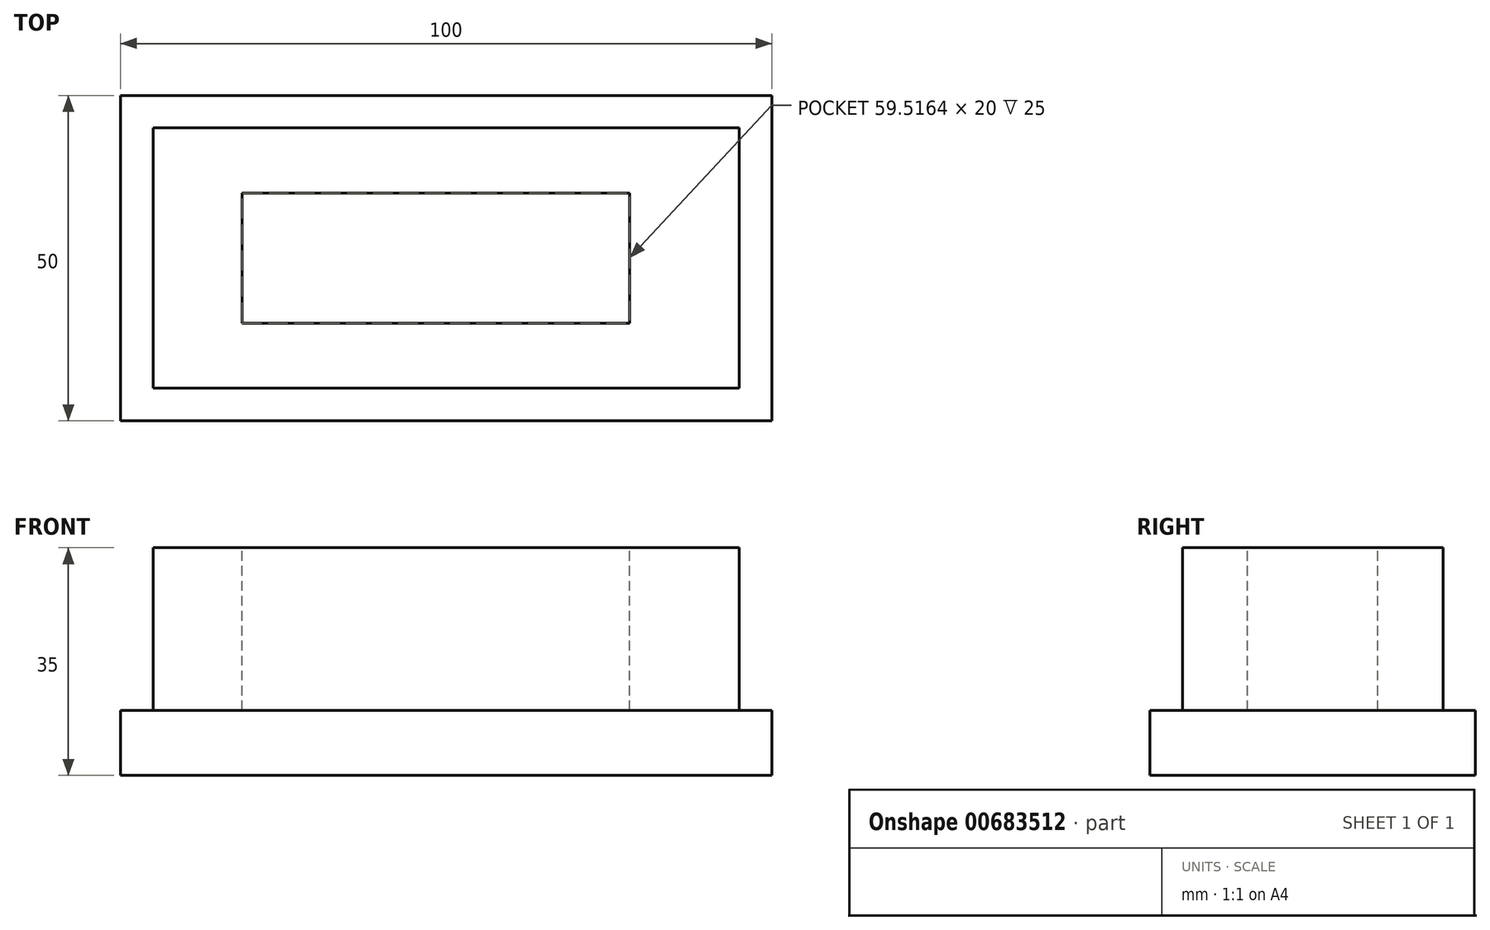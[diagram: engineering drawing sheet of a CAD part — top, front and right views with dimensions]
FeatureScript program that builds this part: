
annotation { "Feature Type Name" : "Feature", "Feature Type Description" : "" }
export const myFeature = defineFeature(function(context is Context, id is Id, definition is map)
    precondition{}
    {
        {
            var Q0;
            Q0=qCreatedBy(makeId("Top.planeOp"),FACE);
            var sketch = newSketch(context, id + "F0", { "sketchPlane" : qUnion([Q0])});
            skLineSegment(sketch, "E0.bottom", {"start": v(-50.38, -7.52) * mm, "end": v(49.62, -7.52) * mm});
            skLineSegment(sketch, "E0.top", {"start": v(-50.38, -57.52) * mm, "end": v(49.62, -57.52) * mm});
            skLineSegment(sketch, "E0.left", {"start": v(-50.38, -7.52) * mm, "end": v(-50.38, -57.52) * mm});
            skLineSegment(sketch, "E0.right", {"start": v(49.62, -7.52) * mm, "end": v(49.62, -57.52) * mm});
            skSolve(sketch);
        }
        {
            var Q0;
            Q0 = qSketchRegion(id + "F0", true);
            extrude(context, id + "F1", {"entities" : qUnion([Q0]), "depth" : 10 * mm, "offsetDistance" : 25 * mm});
        }
        {
            var Q0;
            Q0=makeQuery(id+"F1.opExtrude","CAP_FACE",FACE,{"disambiguationData":[OSD([sQuery(id+"F0.wireOp",EDGE,"E0.bottom"),sQuery(id+"F0.wireOp",EDGE,"E0.top"),sQuery(id+"F0.wireOp",EDGE,"E0.left"),sQuery(id+"F0.wireOp",EDGE,"E0.right")])],"isStart":false});
            var sketch = newSketch(context, id + "F2", { "sketchPlane" : qUnion([Q0])});
            skLineSegment(sketch, "E1.bottom", {"start": v(-45.38, -12.52) * mm, "end": v(44.62, -12.52) * mm});
            skLineSegment(sketch, "E1.top", {"start": v(-45.38, -52.52) * mm, "end": v(44.62, -52.52) * mm});
            skLineSegment(sketch, "E1.left", {"start": v(-45.38, -12.52) * mm, "end": v(-45.38, -52.52) * mm});
            skLineSegment(sketch, "E1.right", {"start": v(44.62, -12.52) * mm, "end": v(44.62, -52.52) * mm});
            skSolve(sketch);
        }
        {
            var Q0;
            Q0=makeQuery(id+"F2.imprint","IMPRINT",FACE,{"disambiguationData":[TD([[makeQuery(id+"F2.imprint","IMPRINT",EDGE,{"derivedFrom":sQuery(id+"F2.wireOp",EDGE,"E1.bottom")}),-1.0]])]});
            extrude(context, id + "F3", {"entities" : qUnion([Q0]), "operationType" : NewBodyOperationType.ADD, "depth" : 5 * mm, "offsetDistance" : 25 * mm});
        }
        {
            var Q0;
            Q0=makeQuery(id+"F2.imprint","IMPRINT",FACE,{"disambiguationData":[TD([[makeQuery(id+"F2.imprint","IMPRINT",EDGE,{"derivedFrom":sQuery(id+"F2.wireOp",EDGE,"E1.bottom")}),-1.0]])]});
            extrude(context, id + "F4", {"entities" : qUnion([Q0]), "operationType" : NewBodyOperationType.ADD, "depth" : 25 * mm, "offsetDistance" : 25 * mm});
        }
        {
            var Q0;
            Q0=makeQuery(id+"F4.opExtrude","CAP_FACE",FACE,{"disambiguationData":[OSD([sQuery(id+"F2.wireOp",EDGE,"E1.bottom"),sQuery(id+"F2.wireOp",EDGE,"E1.top"),sQuery(id+"F2.wireOp",EDGE,"E1.left"),sQuery(id+"F2.wireOp",EDGE,"E1.right")])],"isStart":false});
            var sketch = newSketch(context, id + "F5", { "sketchPlane" : qUnion([Q0])});
            skLineSegment(sketch, "E2.bottom", {"start": v(-31.73, -22.52) * mm, "end": v(27.78, -22.52) * mm});
            skLineSegment(sketch, "E2.top", {"start": v(-31.73, -42.52) * mm, "end": v(27.78, -42.52) * mm});
            skLineSegment(sketch, "E2.left", {"start": v(-31.73, -22.52) * mm, "end": v(-31.73, -42.52) * mm});
            skLineSegment(sketch, "E2.right", {"start": v(27.78, -22.52) * mm, "end": v(27.78, -42.52) * mm});
            skSolve(sketch);
        }
        {
            var Q0;
            Q0=makeQuery(id+"F5.imprint","IMPRINT",FACE,{"disambiguationData":[TD([[makeQuery(id+"F5.imprint","IMPRINT",EDGE,{"derivedFrom":sQuery(id+"F5.wireOp",EDGE,"E2.bottom")}),-1.0]])]});
            extrude(context, id + "F6", {"entities" : qUnion([Q0]), "operationType" : NewBodyOperationType.REMOVE, "oppositeDirection" : true, "depth" : 25 * mm, "offsetDistance" : 25 * mm});
        }
    });
